# Revit family: Air_Gap-Zurn_Wilikns_Model_AG-4 thru AG-8
name_source: partatom
category: Pipe Accessories
units: mm (PartAtom-declared; Revit-internal decimal feet)

## family parameters
Always vertical = Yes
Cut with Voids When Loaded = No
OmniClass Number = 23.65.55.14
OmniClass Title = Valves for Liquid Services
Part Type = Valve - Breaks Into
Round Connector Dimension = Use Radius
Shared = No
Work Plane-Based = No

## types (9) — shared parameters
Assembly Code = D2020300
Bolt Width = 0' - 0 3/16"
Bolt hole Dia = 0' - 0 1/4"
Bush Height = 0' - 0 1/8"
Default Elevation = 0' - 0"
Description = Air Gap Adaptor Fitting
Flow Rate (GPM) = 0 GPM
Height = 1' - 0"
Length = 2' - 0"
Main Material = Paint - Zurn - Cast Grey Iron - Blue
Manufacturer = Zurn Water, LLC
Manufacturer Brand = Zurn Wilkins
Max Working Water Pressure = 0.00 psi
Max Working Water Temperature = 0 °F
Modified Date = 06/18/2025
Product Documentation Link = https://files.zurn.com
Product Page URL = https://www.zurn.com
Product data URL = https://bimobject.com
URL = www.zurn.com/

## per-type parameters (varying)
| type | Arm width | Base Circle OD | Base Height | Bolt circle from End | Bolt hole Bush Dia | Cut Height | DIM A | DIM B TOTAL LENGTH | DIM C INNER DIAMETER | MR Dia | Model | Nominal Diameter | Nominal Radius | OUTER RADIUS | PIPE Max Radius | Product Weight (lbs) | Thickness | Top Cut Radius | Top Cut center | Top End Height | Top End Length | Top End Width |
| AG-8 (1/4” – 1/2” 975XL & 975XL2 Air Gap) | 0' - 0 1/2" | 0' - 1 3/4" | 0' - 0 11/16" | 0' - 0 1/4" | 0' - 0 1/2" | 0' - 1 3/4" | 0' - 2 1/2" | 0' - 3 1/2" | 0' - 1" | 0' - 2 3/4" | AG-8 | 0' - 1" | 0' - 0 1/2" | 0' - 0 7/8" | 0' - 1 1/4" | 2 | 0' - 0 1/8" | 0' - 0 3/4" | 0' - 0 13/32" | 0' - 0 1/2" | 0' - 1 1/2" | 0' - 1 5/16" |
| AG-4 (3/4"-1" 975XL & 975XL2 Air Gap) | 0' - 0 1/2" | 0' - 1 3/4" | 0' - 0 19/32" | 0' - 0 11/32" | 0' - 0 5/8" | 0' - 2 11/16" | 0' - 3 1/4" | 0' - 5" | 0' - 1" | 0' - 3 1/2" | AG-4 | 0' - 1" | 0' - 0 1/2" | 0' - 0 7/8" | 0' - 1 5/8" | 2 | 0' - 0 3/16" | 0' - 0 13/16" | 0' - 0 9/16" | 0' - 0 11/16" | 0' - 1 11/16" | 0' - 1 13/32" |
| AG-5 (1 1/4" - 2" 975XL & 975XL2 Air Gap) | 0' - 0 3/4" | 0' - 3" | 0' - 0 3/4" | 0' - 0 11/32" | 0' - 0 5/8" | 0' - 4 3/4" | 0' - 4 1/2" | 0' - 8" | 0' - 2" | 0' - 4 3/4" | AG-5 | 0' - 2" | 0' - 1" | 0' - 1 1/2" | 0' - 2 1/4" | 3 | 0' - 0 1/4" | 0' - 0 13/16" | 0' - 0 9/16" | 0' - 0 3/4" | 0' - 2 1/8" | 0' - 2" |
| AG-6 (2 1/2" - 3" 475V Air Gap) | 0' - 1" | 0' - 4 1/4" | 0' - 1 1/4" | 0' - 0 11/32" | 0' - 0 5/8" | 0' - 6 1/4" | 0' - 5 3/8" | 0' - 10" | 0' - 3" | 0' - 5 5/8" | AG-6 | 0' - 3" | 0' - 1 1/2" | 0' - 2 1/8" | 0' - 2 11/16" | 5 | 0' - 0 1/4" | 0' - 1 19/32" | 0' - 1 5/16" | 0' - 0 13/16" | 0' - 3" | 0' - 2 1/8" |
| AG-7 (8"-10" 375 & 475 Air Gap) | 0' - 1" | 0' - 5 1/2" | 0' - 1 1/4" | 0' - 0 11/32" | 0' - 0 5/8" | 0' - 6 1/2" | 0' - 7" | 0' - 11" | 0' - 4" | 0' - 7 1/4" | AG-7 | 0' - 4" | 0' - 2" | 0' - 2 3/4" | 0' - 3 1/2" | 8 | 0' - 0 1/4" | 0' - 1 21/32" | 0' - 1 11/32" | 0' - 0 27/32" | 0' - 3 29/32" | 0' - 2 1/8" |
| AG-4 (1 1/4"-1 1/2" 975XL3 Air Gap) | 0' - 0 1/2" | 0' - 1 3/4" | 0' - 0 19/32" | 0' - 0 11/32" | 0' - 0 5/8" | 0' - 2 11/16" | 0' - 3 1/4" | 0' - 5" | 0' - 1" | 0' - 3 1/2" | AG-4 | 0' - 1" | 0' - 0 1/2" | 0' - 0 7/8" | 0' - 1 5/8" | 2 | 0' - 0 3/16" | 0' - 0 13/16" | 0' - 0 9/16" | 0' - 0 11/16" | 0' - 1 11/16" | 0' - 1 13/32" |
| AG-8 (1/2” – 1” 975XL3 Air Gap) | 0' - 0 1/2" | 0' - 1 3/4" | 0' - 0 11/16" | 0' - 0 1/4" | 0' - 0 1/2" | 0' - 1 3/4" | 0' - 2 1/2" | 0' - 3 1/2" | 0' - 1" | 0' - 2 3/4" | AG-8 | 0' - 1" | 0' - 0 1/2" | 0' - 0 7/8" | 0' - 1 1/4" | 2 | 0' - 0 1/8" | 0' - 0 3/4" | 0' - 0 13/32" | 0' - 0 1/2" | 0' - 1 1/2" | 0' - 1 5/16" |
| AG-5 (2" 975XL3 Air Gap) | 0' - 0 3/4" | 0' - 3" | 0' - 0 3/4" | 0' - 0 11/32" | 0' - 0 5/8" | 0' - 4 3/4" | 0' - 4 1/2" | 0' - 8" | 0' - 2" | 0' - 4 3/4" | AG-5 | 0' - 2" | 0' - 1" | 0' - 1 1/2" | 0' - 2 1/4" | 3 | 0' - 0 1/4" | 0' - 0 13/16" | 0' - 0 9/16" | 0' - 0 3/4" | 0' - 2 1/8" | 0' - 2" |
| AG-6 (2 1/2" - 6" 375 & 475 Air Gap) | 0' - 1" | 0' - 4 1/4" | 0' - 1 1/4" | 0' - 0 11/32" | 0' - 0 5/8" | 0' - 6 1/4" | 0' - 5 3/8" | 0' - 10" | 0' - 3" | 0' - 5 5/8" | AG-6 | 0' - 3" | 0' - 1 1/2" | 0' - 2 1/8" | 0' - 2 11/16" | 5 | 0' - 0 1/4" | 0' - 1 19/32" | 0' - 1 5/16" | 0' - 0 13/16" | 0' - 3" | 0' - 2 1/8" |

## geometry (parser evidence)
native form markers: Sweep x2
no freeform markers — native parametric forms only
